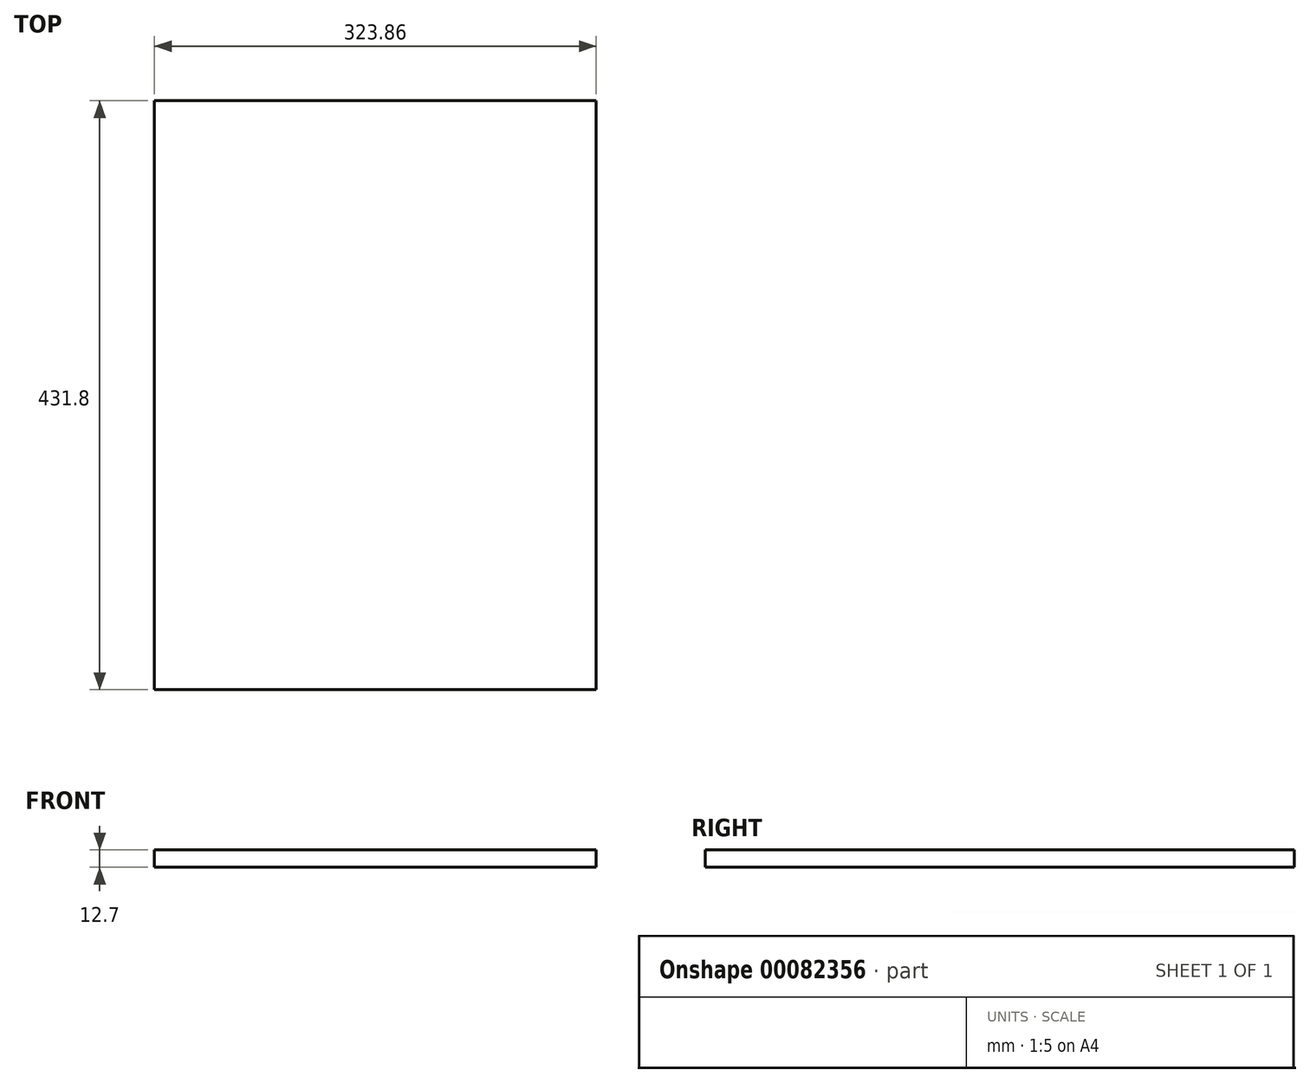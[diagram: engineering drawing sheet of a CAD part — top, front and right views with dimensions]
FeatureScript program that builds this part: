
annotation { "Feature Type Name" : "Feature", "Feature Type Description" : "" }
export const myFeature = defineFeature(function(context is Context, id is Id, definition is map)
    precondition{}
    {
        {
            var Q0;
            Q0=qCreatedBy(makeId("Front.planeOp"),FACE);
            var sketch = newSketch(context, id + "F0", { "sketchPlane" : qUnion([Q0])});
            skLineSegment(sketch, "E0.bottom", {"start": v(161.93, 6.35) * mm, "end": v(-161.93, 6.35) * mm});
            skLineSegment(sketch, "E0.top", {"start": v(161.92, -6.35) * mm, "end": v(-161.92, -6.35) * mm});
            skLineSegment(sketch, "E0.left", {"start": v(161.93, 6.35) * mm, "end": v(161.93, -6.35) * mm});
            skLineSegment(sketch, "E0.right", {"start": v(-161.93, 6.35) * mm, "end": v(-161.93, -6.35) * mm});
            skPoint(sketch, "E0.middle", {"position": v(0, 0) * mm});
            skSolve(sketch);
        }
        {
            var Q0;
            Q0 = qSketchRegion(id + "F0", true);
            extrude(context, id + "F1", {"entities" : qUnion([Q0]), "depth" : 431.8 * mm, "symmetric" : true});
        }
    });
